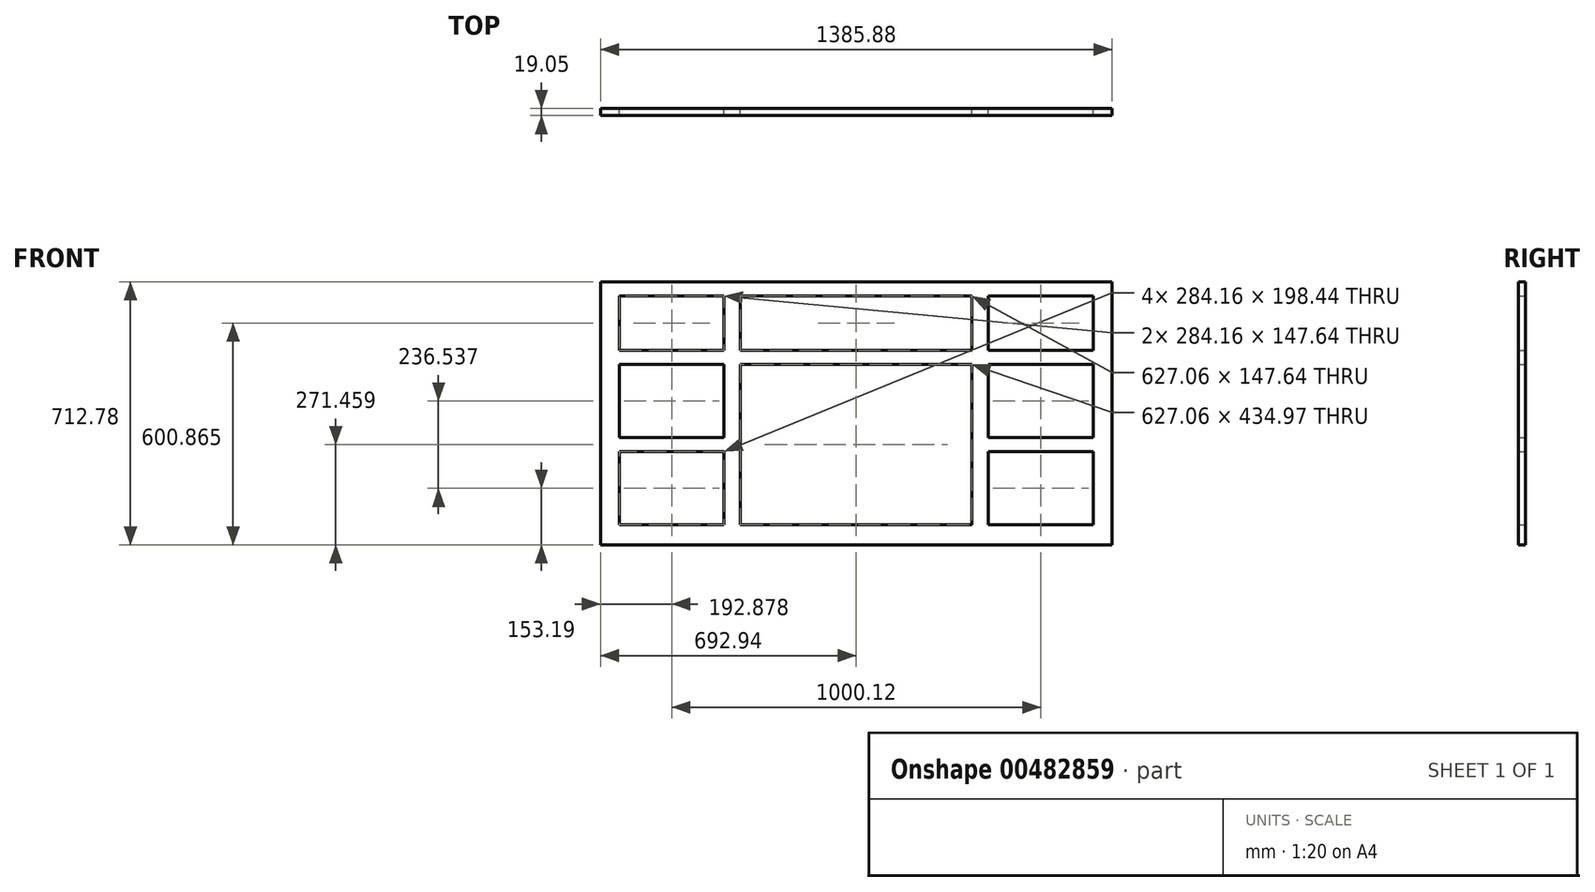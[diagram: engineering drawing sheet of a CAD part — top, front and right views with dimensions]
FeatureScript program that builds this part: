
annotation { "Feature Type Name" : "Feature", "Feature Type Description" : "" }
export const myFeature = defineFeature(function(context is Context, id is Id, definition is map)
    precondition{}
    {
        {
            var Q0;
            Q0=qCreatedBy(makeId("Front.planeOp"),FACE);
            var sketch = newSketch(context, id + "F0", { "sketchPlane" : qUnion([Q0])});
            skLineSegment(sketch, "E0.bottom", {"start": v(692.94, 356.4) * mm, "end": v(-692.94, 356.4) * mm});
            skLineSegment(sketch, "E0.top", {"start": v(692.94, -356.4) * mm, "end": v(-692.94, -356.4) * mm});
            skLineSegment(sketch, "E0.left", {"start": v(692.94, 356.4) * mm, "end": v(692.94, -356.4) * mm});
            skLineSegment(sketch, "E0.right", {"start": v(-692.94, 356.4) * mm, "end": v(-692.94, -356.4) * mm});
            skPoint(sketch, "E0.middle", {"position": v(0, 0) * mm});
            skLineSegment(sketch, "E1.bottom", {"start": v(-642.14, 318.3) * mm, "end": v(-357.98, 318.3) * mm});
            skLineSegment(sketch, "E1.top", {"start": v(-642.14, 170.66) * mm, "end": v(-357.98, 170.66) * mm});
            skLineSegment(sketch, "E1.left", {"start": v(-642.14, 318.3) * mm, "end": v(-642.14, 170.66) * mm});
            skLineSegment(sketch, "E1.right", {"start": v(-357.98, 318.3) * mm, "end": v(-357.98, 170.66) * mm});
            skLineSegment(sketch, "E2.bottom", {"start": v(-642.14, 132.56) * mm, "end": v(-357.98, 132.56) * mm});
            skLineSegment(sketch, "E2.top", {"start": v(-642.14, -65.88) * mm, "end": v(-357.98, -65.88) * mm});
            skLineSegment(sketch, "E2.left", {"start": v(-642.14, 132.56) * mm, "end": v(-642.14, -65.88) * mm});
            skLineSegment(sketch, "E2.right", {"start": v(-357.98, 132.56) * mm, "end": v(-357.98, -65.88) * mm});
            skLineSegment(sketch, "E3.bottom", {"start": v(-642.14, -103.98) * mm, "end": v(-357.98, -103.98) * mm});
            skLineSegment(sketch, "E3.top", {"start": v(-642.14, -302.42) * mm, "end": v(-357.98, -302.42) * mm});
            skLineSegment(sketch, "E3.left", {"start": v(-642.14, -103.98) * mm, "end": v(-642.14, -302.42) * mm});
            skLineSegment(sketch, "E3.right", {"start": v(-357.98, -103.98) * mm, "end": v(-357.98, -302.42) * mm});
            skLineSegment(sketch, "E4.bottom", {"start": v(-313.53, 318.3) * mm, "end": v(313.53, 318.3) * mm});
            skLineSegment(sketch, "E4.top", {"start": v(-313.53, 170.66) * mm, "end": v(313.53, 170.66) * mm});
            skLineSegment(sketch, "E4.left", {"start": v(-313.53, 318.3) * mm, "end": v(-313.53, 170.66) * mm});
            skLineSegment(sketch, "E4.right", {"start": v(313.53, 318.3) * mm, "end": v(313.53, 170.66) * mm});
            skLineSegment(sketch, "E5.bottom", {"start": v(357.98, 318.3) * mm, "end": v(642.14, 318.3) * mm});
            skLineSegment(sketch, "E5.top", {"start": v(357.98, 170.66) * mm, "end": v(642.14, 170.66) * mm});
            skLineSegment(sketch, "E5.left", {"start": v(357.98, 318.3) * mm, "end": v(357.98, 170.66) * mm});
            skLineSegment(sketch, "E5.right", {"start": v(642.14, 318.3) * mm, "end": v(642.14, 170.66) * mm});
            skLineSegment(sketch, "E6.bottom", {"start": v(357.98, 132.56) * mm, "end": v(642.14, 132.56) * mm});
            skLineSegment(sketch, "E6.top", {"start": v(357.98, -65.88) * mm, "end": v(642.14, -65.88) * mm});
            skLineSegment(sketch, "E6.left", {"start": v(357.98, 132.56) * mm, "end": v(357.98, -65.88) * mm});
            skLineSegment(sketch, "E6.right", {"start": v(642.14, 132.56) * mm, "end": v(642.14, -65.88) * mm});
            skLineSegment(sketch, "E7.bottom", {"start": v(357.98, -103.98) * mm, "end": v(642.14, -103.98) * mm});
            skLineSegment(sketch, "E7.top", {"start": v(357.98, -302.42) * mm, "end": v(642.14, -302.42) * mm});
            skLineSegment(sketch, "E7.left", {"start": v(357.98, -103.98) * mm, "end": v(357.98, -302.42) * mm});
            skLineSegment(sketch, "E7.right", {"start": v(642.14, -103.98) * mm, "end": v(642.14, -302.42) * mm});
            skLineSegment(sketch, "E8.bottom", {"start": v(-313.53, 132.56) * mm, "end": v(313.53, 132.56) * mm});
            skLineSegment(sketch, "E8.top", {"start": v(-313.53, -302.42) * mm, "end": v(313.53, -302.42) * mm});
            skLineSegment(sketch, "E8.left", {"start": v(-313.53, 132.56) * mm, "end": v(-313.53, -302.42) * mm});
            skLineSegment(sketch, "E8.right", {"start": v(313.53, 132.56) * mm, "end": v(313.53, -302.42) * mm});
            skSolve(sketch);
        }
        {
            var Q0;
            Q0=makeQuery(id+"F0.imprint","IMPRINT",FACE,{"disambiguationData":[TD([[makeQuery(id+"F0.imprint","IMPRINT",EDGE,{"derivedFrom":sQuery(id+"F0.wireOp",EDGE,"E0.bottom")}),1.0]])]});
            extrude(context, id + "F1", {"entities" : qUnion([Q0]), "depth" : 19.05 * mm});
        }
    });
